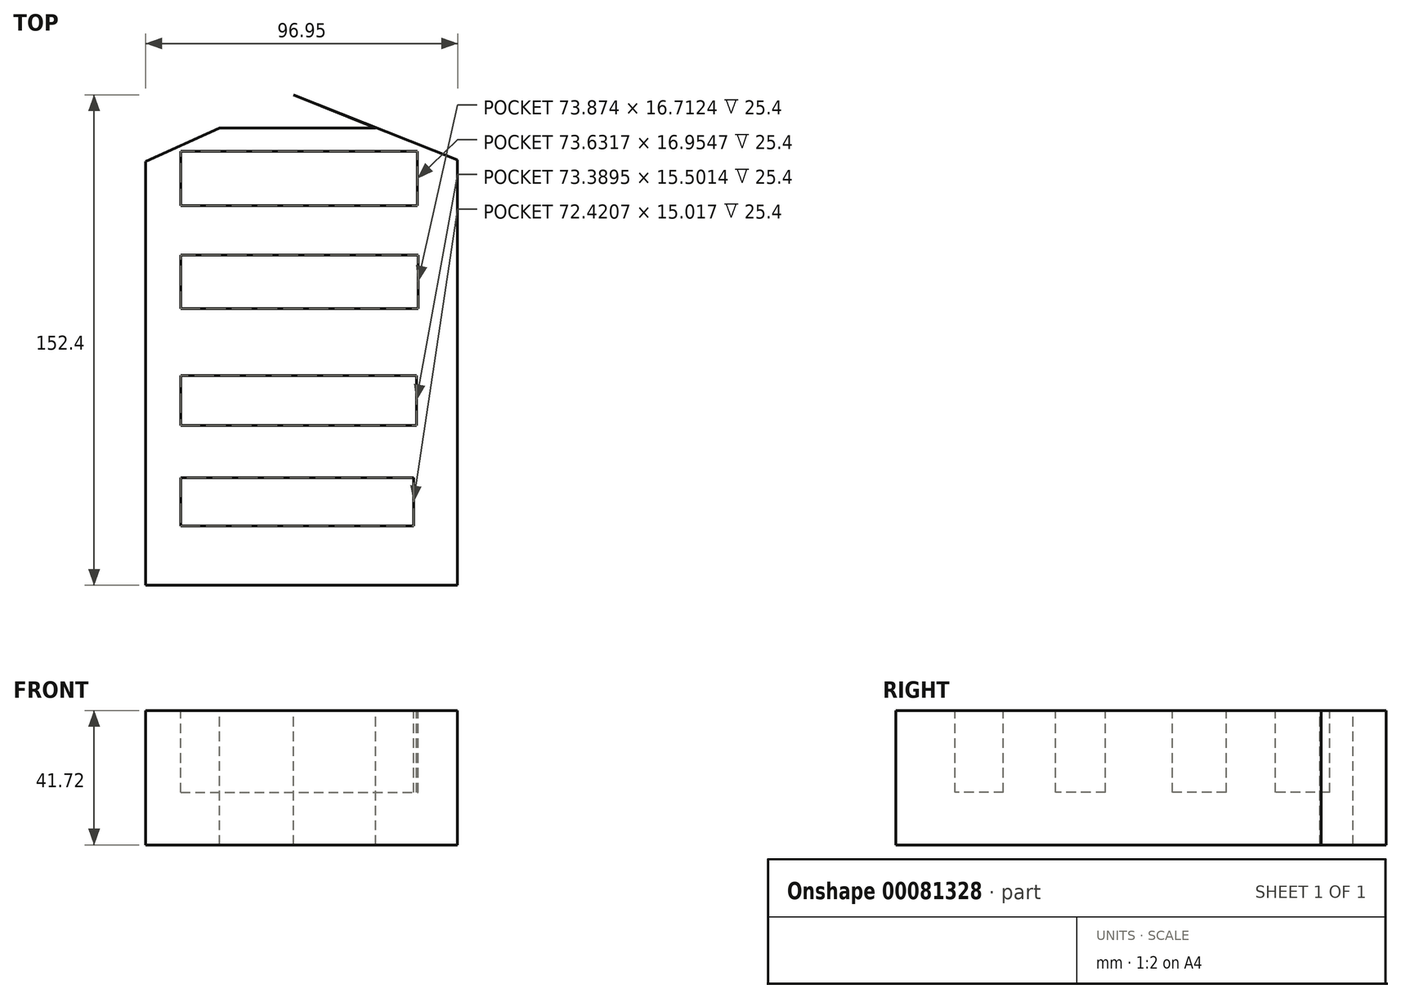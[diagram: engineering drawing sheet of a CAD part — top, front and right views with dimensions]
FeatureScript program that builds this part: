
annotation { "Feature Type Name" : "Feature", "Feature Type Description" : "" }
export const myFeature = defineFeature(function(context is Context, id is Id, definition is map)
    precondition{}
    {
        {
            var Q0;
            Q0=qCreatedBy(makeId("Front.planeOp"),FACE);
            var sketch = newSketch(context, id + "F0", { "sketchPlane" : qUnion([Q0])});
            skLineSegment(sketch, "E0.bottom", {"start": v(-64.92, 14.45) * mm, "end": v(64.3, 14.45) * mm});
            skLineSegment(sketch, "E0.top", {"start": v(-64.92, -27.27) * mm, "end": v(64.3, -27.27) * mm});
            skLineSegment(sketch, "E0.left", {"start": v(-64.92, 14.45) * mm, "end": v(-64.92, -27.27) * mm});
            skLineSegment(sketch, "E0.right", {"start": v(64.3, 14.45) * mm, "end": v(64.3, -27.27) * mm});
            skSolve(sketch);
        }
        {
            var Q0;
            Q0=makeQuery(id+"F0.imprint","IMPRINT",FACE,{"disambiguationData":[TD([[makeQuery(id+"F0.imprint","IMPRINT",EDGE,{"derivedFrom":sQuery(id+"F0.wireOp",EDGE,"E0.bottom")}),-1.0]])]});
            extrude(context, id + "F1", {"entities" : qUnion([Q0]), "depth" : 152.4 * mm});
        }
        {
            var Q0;
            Q0=makeQuery(id+"F1.opExtrude","SWEPT_FACE",FACE,{"disambiguationData":[OSD([sQuery(id+"F0.wireOp",EDGE,"E0.bottom")])]});
            var sketch = newSketch(context, id + "F2", { "sketchPlane" : qUnion([Q0])});
            skLineSegment(sketch, "E1.bottom", {"start": v(-35.12, -17.51) * mm, "end": v(38.51, -17.51) * mm});
            skLineSegment(sketch, "E1.top", {"start": v(-35.12, -34.47) * mm, "end": v(38.51, -34.47) * mm});
            skLineSegment(sketch, "E1.left", {"start": v(-35.12, -17.51) * mm, "end": v(-35.12, -34.47) * mm});
            skLineSegment(sketch, "E1.right", {"start": v(38.51, -17.51) * mm, "end": v(38.51, -34.47) * mm});
            skLineSegment(sketch, "E2.bottom", {"start": v(-35.12, -49.73) * mm, "end": v(38.75, -49.73) * mm});
            skLineSegment(sketch, "E2.top", {"start": v(-35.12, -66.44) * mm, "end": v(38.75, -66.44) * mm});
            skLineSegment(sketch, "E2.left", {"start": v(-35.12, -49.73) * mm, "end": v(-35.12, -66.44) * mm});
            skLineSegment(sketch, "E2.right", {"start": v(38.75, -49.73) * mm, "end": v(38.75, -66.44) * mm});
            skSolve(sketch);
        }
        {
            var Q0;
            Q0=makeQuery(id+"F2.imprint","IMPRINT",FACE,{"disambiguationData":[TD([[makeQuery(id+"F2.imprint","IMPRINT",EDGE,{"derivedFrom":sQuery(id+"F2.wireOp",EDGE,"E1.bottom")}),-1.0]])]});
            var Q1;
            Q1=makeQuery(id+"F2.imprint","IMPRINT",FACE,{"disambiguationData":[TD([[makeQuery(id+"F2.imprint","IMPRINT",EDGE,{"derivedFrom":sQuery(id+"F2.wireOp",EDGE,"E2.bottom")}),-1.0]])]});
            extrude(context, id + "F3", {"entities" : qUnion([Q0, Q1]), "operationType" : NewBodyOperationType.REMOVE, "oppositeDirection" : true, "depth" : 25.4 * mm});
        }
        {
            var Q0;
            Q0=makeQuery(id+"F1.opExtrude","SWEPT_FACE",FACE,{"disambiguationData":[OSD([sQuery(id+"F0.wireOp",EDGE,"E0.bottom")])]});
            var sketch = newSketch(context, id + "F4", { "sketchPlane" : qUnion([Q0])});
            skLineSegment(sketch, "E3", {"start": v(-64.92, -29.2) * mm, "end": v(0, 0) * mm});
            skLineSegment(sketch, "E4", {"start": v(0, 0) * mm, "end": v(64.3, -25.48) * mm});
            skSolve(sketch);
        }
        {
            var Q0;
            {var subQ0=sQuery(id+"F4.wireOp",EDGE,"E4");Q0=makeQuery(id+"F4.imprint","IMPRINT",FACE,{"disambiguationData":[TD([[makeQuery(id+"F4.imprint","IMPRINT",EDGE,{"derivedFrom":subQ0}),1.0]])]});}
            var Q1;
            {var subQ0=sQuery(id+"F4.wireOp",EDGE,"E3");Q1=makeQuery(id+"F4.imprint","IMPRINT",FACE,{"disambiguationData":[TD([[makeQuery(id+"F4.imprint","IMPRINT",EDGE,{"derivedFrom":subQ0}),1.0]])]});}
            extrude(context, id + "F5", {"entities" : qUnion([Q0, Q1]), "operationType" : NewBodyOperationType.REMOVE, "endBound" : BoundingType.THROUGH_ALL, "oppositeDirection" : true, "depth" : 25.4 * mm});
        }
        {
            var Q0;
            Q0=makeQuery(id+"F1.opExtrude","SWEPT_FACE",FACE,{"disambiguationData":[OSD([sQuery(id+"F0.wireOp",EDGE,"E0.bottom")])]});
            var sketch = newSketch(context, id + "F6", { "sketchPlane" : qUnion([Q0])});
            skLineSegment(sketch, "E5.bottom", {"start": v(-35.12, -87.27) * mm, "end": v(38.27, -87.27) * mm});
            skLineSegment(sketch, "E5.top", {"start": v(-35.12, -102.77) * mm, "end": v(38.27, -102.77) * mm});
            skLineSegment(sketch, "E5.left", {"start": v(-35.12, -87.27) * mm, "end": v(-35.12, -102.77) * mm});
            skLineSegment(sketch, "E5.right", {"start": v(38.27, -87.27) * mm, "end": v(38.27, -102.77) * mm});
            skSolve(sketch);
        }
        {
            var Q0;
            Q0=makeQuery(id+"F6.imprint","IMPRINT",FACE,{"disambiguationData":[TD([[makeQuery(id+"F6.imprint","IMPRINT",EDGE,{"derivedFrom":sQuery(id+"F6.wireOp",EDGE,"E5.bottom")}),-1.0]])]});
            extrude(context, id + "F7", {"entities" : qUnion([Q0]), "operationType" : NewBodyOperationType.REMOVE, "oppositeDirection" : true, "depth" : 25.4 * mm});
        }
        {
            var Q0;
            Q0=makeQuery(id+"F1.opExtrude","SWEPT_FACE",FACE,{"disambiguationData":[OSD([sQuery(id+"F0.wireOp",EDGE,"E0.bottom")])]});
            var sketch = newSketch(context, id + "F8", { "sketchPlane" : qUnion([Q0])});
            skLineSegment(sketch, "E6.bottom", {"start": v(-35.12, -119) * mm, "end": v(37.3, -119) * mm});
            skLineSegment(sketch, "E6.top", {"start": v(-35.12, -134.02) * mm, "end": v(37.3, -134.02) * mm});
            skLineSegment(sketch, "E6.left", {"start": v(-35.12, -119) * mm, "end": v(-35.12, -134.02) * mm});
            skLineSegment(sketch, "E6.right", {"start": v(37.3, -119) * mm, "end": v(37.3, -134.02) * mm});
            skSolve(sketch);
        }
        {
            var Q0;
            Q0=makeQuery(id+"F8.imprint","IMPRINT",FACE,{"disambiguationData":[TD([[makeQuery(id+"F8.imprint","IMPRINT",EDGE,{"derivedFrom":sQuery(id+"F8.wireOp",EDGE,"E6.bottom")}),-1.0]])]});
            extrude(context, id + "F9", {"entities" : qUnion([Q0]), "operationType" : NewBodyOperationType.REMOVE, "oppositeDirection" : true, "depth" : 25.4 * mm});
        }
        {
            var Q0;
            Q0=makeQuery(id+"F1.opExtrude","SWEPT_FACE",FACE,{"disambiguationData":[OSD([sQuery(id+"F0.wireOp",EDGE,"E0.bottom")])]});
            var sketch = newSketch(context, id + "F10", { "sketchPlane" : qUnion([Q0])});
            skLineSegment(sketch, "E7", {"start": v(50.99, -20.2) * mm, "end": v(50.99, -152.4) * mm});
            skLineSegment(sketch, "E8", {"start": v(50.99, -152.4) * mm, "end": v(64.3, -25.48) * mm});
            skLineSegment(sketch, "E9", {"start": v(64.3, -25.48) * mm, "end": v(64.3, -152.4) * mm});
            skLineSegment(sketch, "E10", {"start": v(64.3, -152.4) * mm, "end": v(50.99, -152.4) * mm});
            skLineSegment(sketch, "E11", {"start": v(50.99, -20.2) * mm, "end": v(64.3, -25.48) * mm});
            skSolve(sketch);
        }
        {
            var Q0;
            Q0=makeQuery(id+"F10.imprint","IMPRINT",FACE,{"disambiguationData":[TD([[makeQuery(id+"F10.imprint","IMPRINT",EDGE,{"derivedFrom":sQuery(id+"F10.wireOp",EDGE,"E7")}),1.0]])]});
            var Q1;
            Q1=makeQuery(id+"F10.imprint","IMPRINT",FACE,{"disambiguationData":[TD([[makeQuery(id+"F10.imprint","IMPRINT",EDGE,{"derivedFrom":sQuery(id+"F10.wireOp",EDGE,"E8")}),-1.0]])]});
            extrude(context, id + "F11", {"entities" : qUnion([Q0, Q1]), "operationType" : NewBodyOperationType.REMOVE, "oppositeDirection" : true, "depth" : 75.8 * mm});
        }
        {
            var Q0;
            Q0=makeQuery(id+"F1.opExtrude","SWEPT_FACE",FACE,{"disambiguationData":[OSD([sQuery(id+"F0.wireOp",EDGE,"E0.bottom")])]});
            var sketch = newSketch(context, id + "F12", { "sketchPlane" : qUnion([Q0])});
            skLineSegment(sketch, "E12", {"start": v(-45.96, -20.68) * mm, "end": v(-45.96, -152.4) * mm});
            skLineSegment(sketch, "E13", {"start": v(-45.96, -152.4) * mm, "end": v(-64.92, -152.4) * mm});
            skLineSegment(sketch, "E14", {"start": v(-64.92, -152.4) * mm, "end": v(-64.92, -29.2) * mm});
            skLineSegment(sketch, "E15", {"start": v(-64.92, -29.2) * mm, "end": v(-45.96, -20.68) * mm});
            skSolve(sketch);
        }
        {
            var Q0;
            Q0=makeQuery(id+"F12.imprint","IMPRINT",FACE,{"disambiguationData":[TD([[makeQuery(id+"F12.imprint","IMPRINT",EDGE,{"derivedFrom":sQuery(id+"F12.wireOp",EDGE,"E12")}),-1.0]])]});
            extrude(context, id + "F13", {"entities" : qUnion([Q0]), "operationType" : NewBodyOperationType.REMOVE, "oppositeDirection" : true, "depth" : 105.44 * mm});
        }
        {
            var Q0;
            Q0=makeQuery(id+"F1.opExtrude","SWEPT_FACE",FACE,{"disambiguationData":[OSD([sQuery(id+"F0.wireOp",EDGE,"E0.bottom")])]});
            var sketch = newSketch(context, id + "F14", { "sketchPlane" : qUnion([Q0])});
            skLineSegment(sketch, "E16", {"start": v(-22.98, -10.34) * mm, "end": v(25.5, -10.34) * mm});
            skPoint(sketch, "E16.endSnap0", {"position": v(25.5, -10.1) * mm});
            skPoint(sketch, "E16.endSnap1", {"position": v(-22.98, -10.34) * mm});
            skLineSegment(sketch, "E17", {"start": v(25.5, -10.34) * mm, "end": v(0, 0) * mm});
            skLineSegment(sketch, "E18", {"start": v(0, 0) * mm, "end": v(-22.98, -10.34) * mm});
            skSolve(sketch);
        }
        {
            var Q0;
            Q0=makeQuery(id+"F14.imprint","IMPRINT",FACE,{"disambiguationData":[TD([[makeQuery(id+"F14.imprint","IMPRINT",EDGE,{"derivedFrom":sQuery(id+"F14.wireOp",EDGE,"E16")}),1.0]])]});
            extrude(context, id + "F15", {"entities" : qUnion([Q0]), "operationType" : NewBodyOperationType.REMOVE, "oppositeDirection" : true, "depth" : 137.53 * mm});
        }
    });
